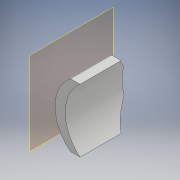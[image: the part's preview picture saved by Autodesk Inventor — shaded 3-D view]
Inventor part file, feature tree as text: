
AUTODESK INVENTOR PART (.ipt)
format: ipt  version: 2018 (Build 220112000, 112)  size: 130,048 bytes
history: native  units: mm
features: extrude x4, sketch x4, plane x1
ambient origin geometry x8: Origin, YZ Plane, XZ Plane, XY Plane, X Axis, Y Axis, Z Axis, Center Point
bodies: Solid1 (feature_tree)
feature tree (9):
  extrude  "Extrusion1"  Depth=12.0mm TaperAngle=0.0deg
  plane  "Work Plane1"
  sketch  "Sketch2"  dims[d8=-10.0mm d9=10.0mm]
  extrude  "Extrusion2"  Depth=10.0mm
  extrude  "Extrusion7"  Depth=6.5mm
  extrude  "Extrusion8"  Depth=10.0mm
  sketch  "Sketch1"  dims[d0=13.0mm d1=12.0mm d2=0.0mm]
  sketch  "Sketch7"  dims[d10=6.5mm d12=4.0mm]
  sketch  "Sketch8"  dims[d14=3.0mm d15=3.0mm d16=10.0mm d17=0.0mm d24=1.5mm d34=10.0mm d35=0.0mm d36=1.5mm d37=1.5mm d38=0.0mm d39=0.0mm]
